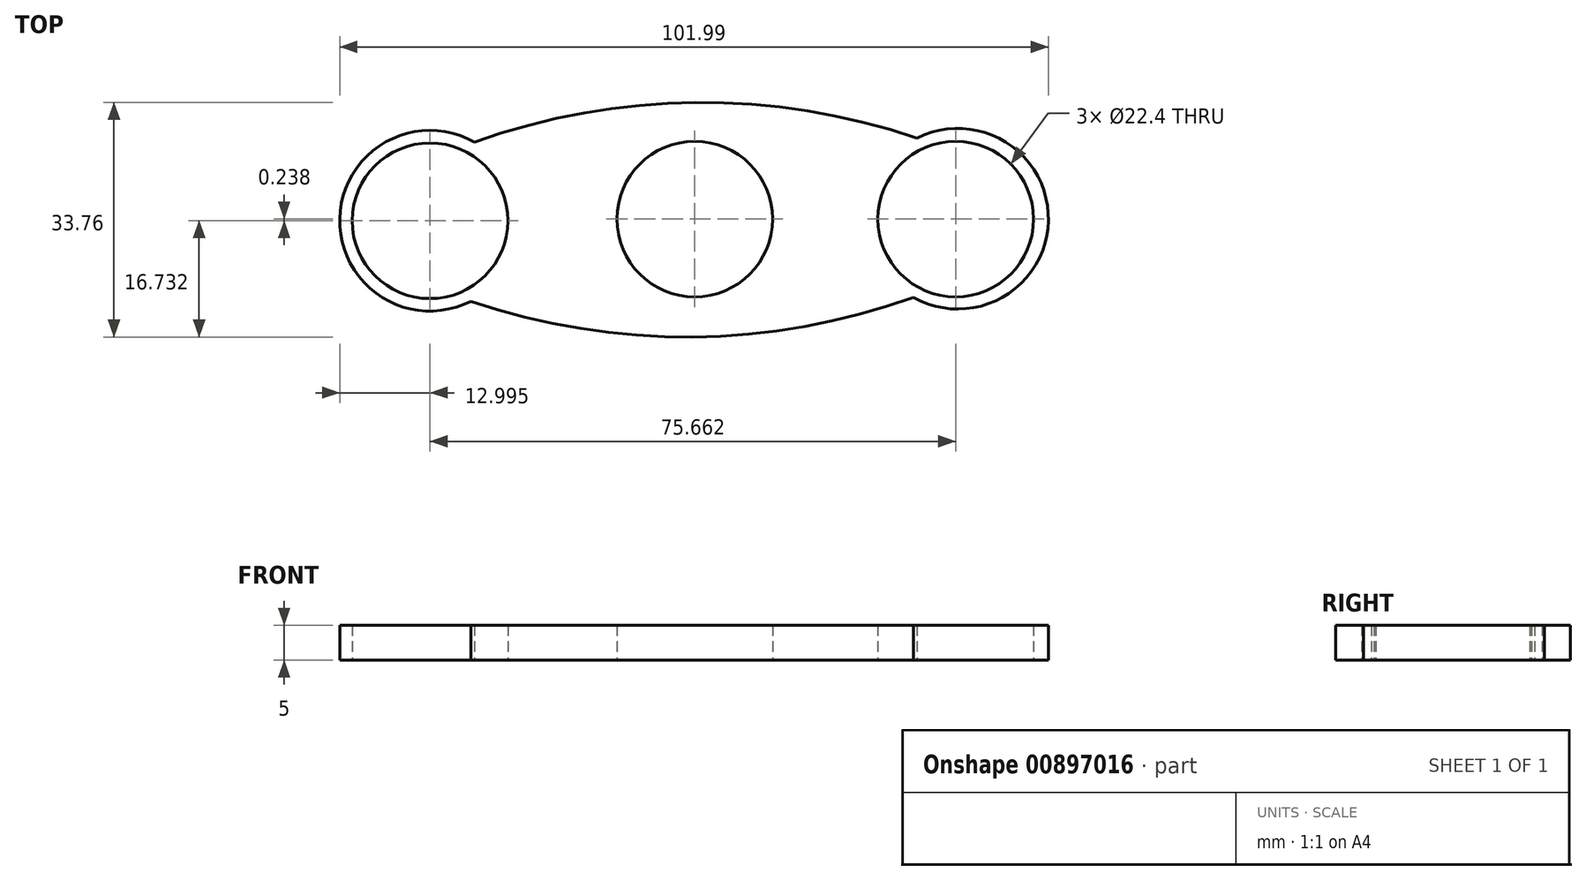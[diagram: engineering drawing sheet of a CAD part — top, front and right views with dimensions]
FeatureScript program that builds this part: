
annotation { "Feature Type Name" : "Feature", "Feature Type Description" : "" }
export const myFeature = defineFeature(function(context is Context, id is Id, definition is map)
    precondition{}
    {
        {
            var Q0;
            Q0=qCreatedBy(makeId("Top.planeOp"),FACE);
            var sketch = newSketch(context, id + "F0", { "sketchPlane" : qUnion([Q0])});
            skCircle(sketch, "E0", {"center": v(0, 0) * mm, "radius": 11.2 * mm});
            skCircle(sketch, "E1", {"center": v(37.56, 0) * mm, "radius": 11.2 * mm});
            skCircle(sketch, "E2.1.0", {"center": v(-38.1, -0.24) * mm, "radius": 11.2 * mm});
            skPoint(sketch, "E2.center", {"position": v(-0.27, -0.12) * mm});
            skCircle(sketch, "E3", {"center": v(-38.1, -0.24) * mm, "radius": 13 * mm});
            skCircle(sketch, "E4.1.0", {"center": v(37.9, 0.05) * mm, "radius": 13 * mm});
            skPoint(sketch, "E4.center", {"position": v(-0.1, -0.1) * mm});
            skArc(sketch, "E5", {"start": v(-32.22, -11.83) * mm, "mid": v(-0.32, -16.97) * mm, "end": v(31.47, -11.25) * mm});
            skArc(sketch, "E6.1.0", {"start": v(32, 11.64) * mm, "mid": v(0.11, 16.78) * mm, "end": v(-31.69, 11.07) * mm});
            skSolve(sketch);
        }
        {
            var Q0;
            Q0=makeQuery(id+"F0.imprint","IMPRINT",FACE,{"disambiguationData":[TD([[makeQuery(id+"F0.imprint","IMPRINT",EDGE,{"derivedFrom":sQuery(id+"F0.wireOp",EDGE,"E0")}),-1.0]])]});
            var Q1;
            Q1=makeQuery(id+"F0.imprint","IMPRINT",FACE,{"disambiguationData":[TD([[makeQuery(id+"F0.imprint","IMPRINT",EDGE,{"derivedFrom":sQuery(id+"F0.wireOp",EDGE,"E2.1.0")}),-1.0]])]});
            var Q2;
            Q2=makeQuery(id+"F0.imprint","IMPRINT",FACE,{"disambiguationData":[TD([[makeQuery(id+"F0.imprint","IMPRINT",EDGE,{"derivedFrom":sQuery(id+"F0.wireOp",EDGE,"E1")}),-1.0]])]});
            extrude(context, id + "F1", {"entities" : qUnion([Q0, Q1, Q2]), "depth" : 5 * mm, "offsetDistance" : 25 * mm});
        }
    });
